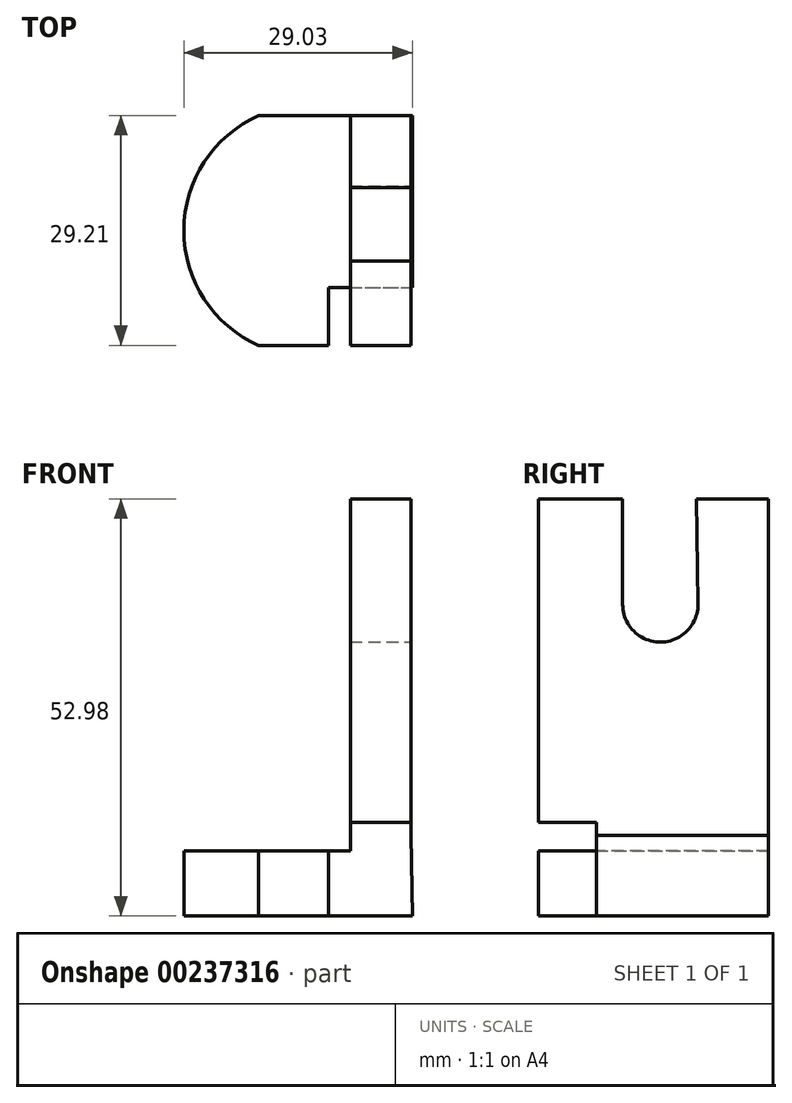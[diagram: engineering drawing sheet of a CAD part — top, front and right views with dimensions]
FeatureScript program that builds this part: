
annotation { "Feature Type Name" : "Feature", "Feature Type Description" : "" }
export const myFeature = defineFeature(function(context is Context, id is Id, definition is map)
    precondition{}
    {
        {
            var Q0;
            Q0=qCreatedBy(makeId("Front.planeOp"),FACE);
            var sketch = newSketch(context, id + "F0", { "sketchPlane" : qUnion([Q0])});
            skLineSegment(sketch, "E0", {"start": v(10.45, -7.24) * mm, "end": v(10.45, 35.47) * mm});
            skLineSegment(sketch, "E1", {"start": v(10.45, 35.47) * mm, "end": v(2.75, 35.47) * mm});
            skLineSegment(sketch, "E2", {"start": v(2.75, 35.47) * mm, "end": v(2.75, -9.24) * mm});
            skLineSegment(sketch, "E3", {"start": v(2.75, -9.24) * mm, "end": v(-20.53, -9.24) * mm});
            skLineSegment(sketch, "E4", {"start": v(-20.53, -9.24) * mm, "end": v(-20.53, -17.5) * mm});
            skLineSegment(sketch, "E5", {"start": v(-20.53, -17.5) * mm, "end": v(10.63, -17.5) * mm});
            skLineSegment(sketch, "E6", {"start": v(10.63, -17.5) * mm, "end": v(10.45, -7.24) * mm});
            skSolve(sketch);
        }
        {
            var Q0;
            Q0=makeQuery(id+"F0.imprint","IMPRINT",FACE,{"disambiguationData":[TD([[makeQuery(id+"F0.imprint","IMPRINT",EDGE,{"derivedFrom":sQuery(id+"F0.wireOp",EDGE,"E0")}),1.0]])]});
            extrude(context, id + "F1", {"entities" : qUnion([Q0]), "depth" : 15.5 * mm, "hasSecondDirection" : true, "secondDirectionOppositeDirection" : true, "secondDirectionDepth" : 13.72 * mm});
        }
        {
            var Q0;
            Q0=makeQuery(id+"F1.opExtrude","SWEPT_FACE",FACE,{"disambiguationData":[OSD([sQuery(id+"F0.wireOp",EDGE,"E0")])]});
            var sketch = newSketch(context, id + "F2", { "sketchPlane" : qUnion([Q0])});
            skCircle(sketch, "E7", {"center": v(0, 22.07) * mm, "radius": 4.78 * mm});
            skLineSegment(sketch, "E8", {"start": v(-4.78, 22.07) * mm, "end": v(-4.78, 35.47) * mm});
            skLineSegment(sketch, "E9", {"start": v(-4.78, 35.47) * mm, "end": v(4.58, 35.47) * mm});
            skLineSegment(sketch, "E10", {"start": v(4.58, 35.47) * mm, "end": v(4.78, 22.07) * mm});
            skSolve(sketch);
        }
        {
            var Q0;
            {var subQ0=sQuery(id+"F2.wireOp",EDGE,"E7");var subQ1=makeQuery(id+"F2.imprint","INTERSECT",VERTEX,{"derivedFrom":[subQ0,sQuery(id+"F2.wireOp",EDGE,"E8")]});Q0=makeQuery(id+"F2.imprint","IMPRINT",FACE,{"disambiguationData":[TD([[makeQuery(id+"F2.imprint","IMPRINT",EDGE,{"disambiguationData":[TD([[subQ1,1.0]])],"derivedFrom":subQ0}),1.0]])]});}
            var Q1;
            {var subQ0=sQuery(id+"F2.wireOp",EDGE,"E8");Q1=makeQuery(id+"F2.imprint","IMPRINT",FACE,{"disambiguationData":[TD([[makeQuery(id+"F2.imprint","IMPRINT",EDGE,{"derivedFrom":subQ0}),-1.0]])]});}
            extrude(context, id + "F3", {"entities" : qUnion([Q0, Q1]), "operationType" : NewBodyOperationType.REMOVE, "oppositeDirection" : true, "depth" : 25.4 * mm});
        }
        {
            var Q0;
            Q0=makeQuery(id+"F1.opExtrude","SWEPT_FACE",FACE,{"disambiguationData":[OSD([sQuery(id+"F0.wireOp",EDGE,"E3")])]});
            var sketch = newSketch(context, id + "F4", { "sketchPlane" : qUnion([Q0])});
            skArc(sketch, "E11", {"start": v(-8.9, 13.72) * mm, "mid": v(-18.4, -0.89) * mm, "end": v(-8.9, -15.5) * mm});
            skSolve(sketch);
        }
        {
            var Q0;
            {var subQ0=sQuery(id+"F4.wireOp",EDGE,"E11");Q0=makeQuery(id+"F4.imprint","IMPRINT",FACE,{"disambiguationData":[TD([[makeQuery(id+"F4.imprint","IMPRINT",EDGE,{"derivedFrom":subQ0}),-1.0]])]});}
            extrude(context, id + "F5", {"entities" : qUnion([Q0]), "operationType" : NewBodyOperationType.REMOVE, "oppositeDirection" : true, "depth" : 25.4 * mm});
        }
        {
            var Q0;
            Q0=makeQuery(id+"F1.opExtrude","CAP_FACE",FACE,{"disambiguationData":[OSD([sQuery(id+"F0.wireOp",EDGE,"E0"),sQuery(id+"F0.wireOp",EDGE,"E1"),sQuery(id+"F0.wireOp",EDGE,"E2"),sQuery(id+"F0.wireOp",EDGE,"E3"),sQuery(id+"F0.wireOp",EDGE,"E4"),sQuery(id+"F0.wireOp",EDGE,"E5"),sQuery(id+"F0.wireOp",EDGE,"E6")])],"isStart":false});
            var sketch = newSketch(context, id + "F6", { "sketchPlane" : qUnion([Q0])});
            skLineSegment(sketch, "E12.bottom", {"start": v(0, -5.6) * mm, "end": v(14.11, -5.6) * mm});
            skLineSegment(sketch, "E12.top", {"start": v(0, -20.8) * mm, "end": v(14.11, -20.8) * mm});
            skLineSegment(sketch, "E12.left", {"start": v(0, -5.6) * mm, "end": v(0, -20.8) * mm});
            skLineSegment(sketch, "E12.right", {"start": v(14.11, -5.6) * mm, "end": v(14.11, -20.8) * mm});
            skSolve(sketch);
        }
        {
            var Q0;
            {var subQ0=makeQuery(id+"F1.opExtrude","CAP_EDGE",EDGE,{"disambiguationData":[OSD([sQuery(id+"F0.wireOp",EDGE,"E6")])],"isStart":false});Q0=makeQuery(id+"F6.imprint","IMPRINT",FACE,{"disambiguationData":[TD([[makeQuery(id+"F6.imprint","IMPRINT",EDGE,{"derivedFrom":subQ0}),1.0]])]});}
            extrude(context, id + "F7", {"entities" : qUnion([Q0]), "operationType" : NewBodyOperationType.REMOVE, "oppositeDirection" : true, "depth" : 7.37 * mm});
        }
    });
